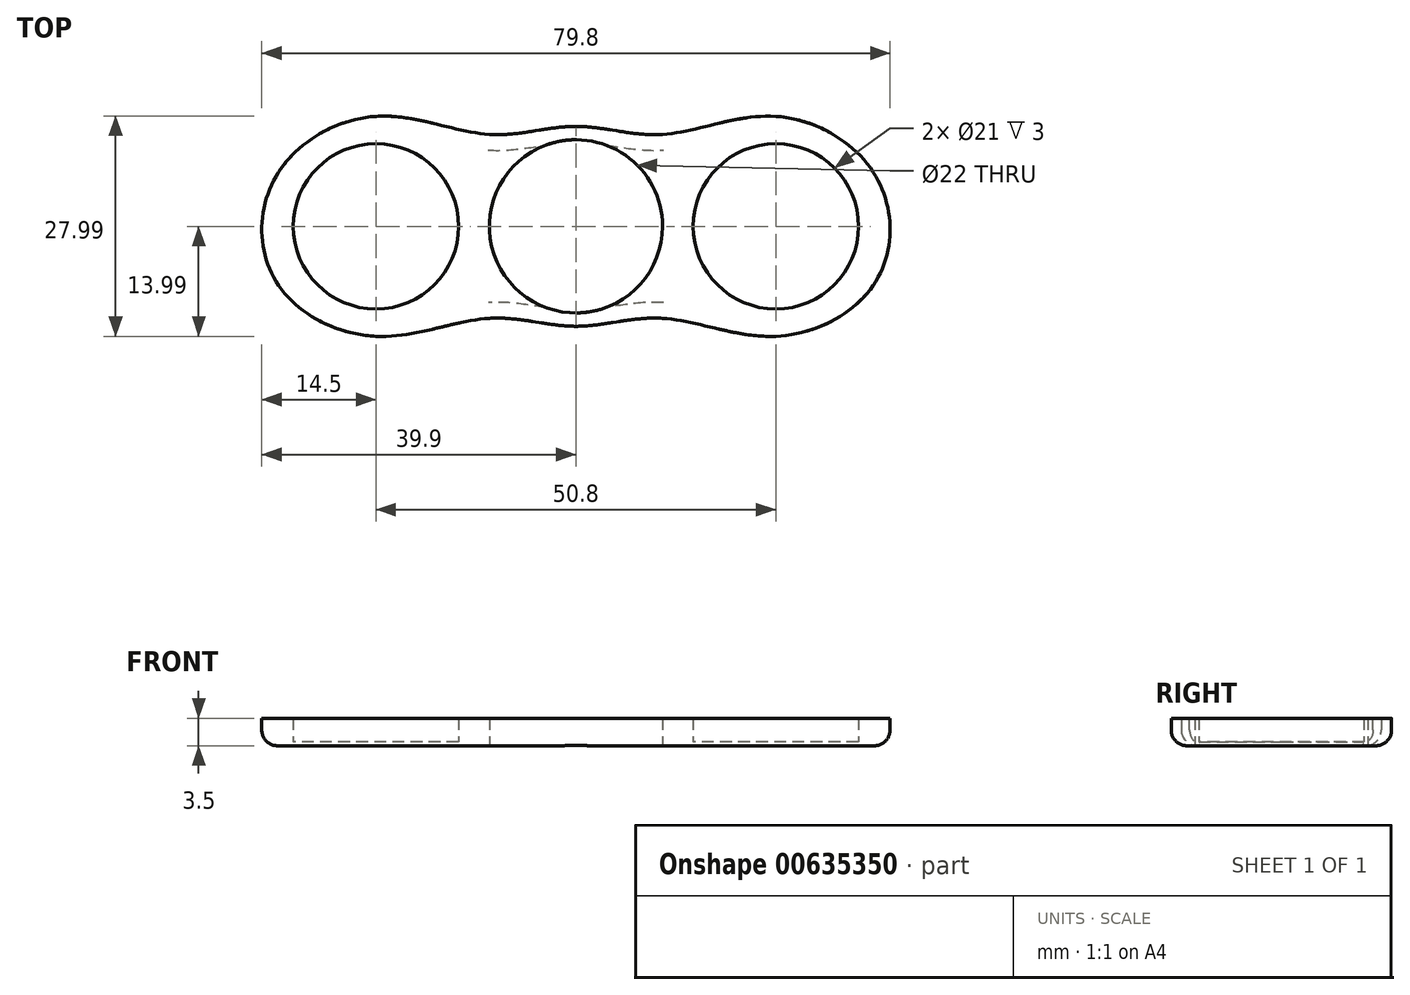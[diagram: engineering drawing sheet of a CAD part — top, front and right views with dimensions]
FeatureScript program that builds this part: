
annotation { "Feature Type Name" : "Feature", "Feature Type Description" : "" }
export const myFeature = defineFeature(function(context is Context, id is Id, definition is map)
    precondition{}
    {
        {
            var Q0;
            Q0=qCreatedBy(makeId("Top.planeOp"),FACE);
            var sketch = newSketch(context, id + "F0", { "sketchPlane" : qUnion([Q0])});
            skCircle(sketch, "E0", {"center": v(0, 0) * mm, "radius": 11 * mm});
            skLineSegment(sketch, "E1", {"start": v(0, 0) * mm, "end": v(25.4, 0) * mm});
            skLineSegment(sketch, "E2", {"start": v(0, 0) * mm, "end": v(-25.4, 0) * mm});
            skCircle(sketch, "E3", {"center": v(-25.4, 0) * mm, "radius": 10.5 * mm});
            skCircle(sketch, "E4", {"center": v(25.4, 0) * mm, "radius": 10.5 * mm});
            skLineSegment(sketch, "E5", {"start": v(-25.4, 0) * mm, "end": v(-25.4, -13.97) * mm});
            skLineSegment(sketch, "E6", {"start": v(25.4, 0) * mm, "end": v(25.4, -13.97) * mm});
            skLineSegment(sketch, "E7", {"start": v(-25.4, 0) * mm, "end": v(-25.4, 13.97) * mm});
            skLineSegment(sketch, "E8", {"start": v(25.4, 0) * mm, "end": v(25.4, 13.97) * mm});
            skLineSegment(sketch, "E9", {"start": v(0, 0) * mm, "end": v(0, -12.7) * mm});
            skLineSegment(sketch, "E10", {"start": v(0, 0) * mm, "end": v(0, 12.7) * mm});
            skLineSegment(sketch, "E11", {"start": v(0, 0) * mm, "end": v(0, -6.98) * mm});
            skPoint(sketch, "E11.endSnap0", {"position": v(25.4, -6.98) * mm});
            skLineSegment(sketch, "E12", {"start": v(0, 0) * mm, "end": v(0, 6.35) * mm});
            skLineSegment(sketch, "E13", {"start": v(0, -6.98) * mm, "end": v(38.1, -6.98) * mm});
            skLineSegment(sketch, "E14", {"start": v(38.1, 6.35) * mm, "end": v(0, 6.35) * mm});
            skLineSegment(sketch, "E15", {"start": v(0, 6.35) * mm, "end": v(-38.1, 6.35) * mm});
            skLineSegment(sketch, "E16", {"start": v(0, -6.98) * mm, "end": v(-38.1, -6.98) * mm});
            skLineSegment(sketch, "E17", {"start": v(-11, 0) * mm, "end": v(-11, -11.68) * mm});
            skPoint(sketch, "E17.startSnap0", {"position": v(-12.7, 0) * mm});
            skLineSegment(sketch, "E18", {"start": v(-11, -11.68) * mm, "end": v(-11, 0) * mm});
            skLineSegment(sketch, "E19", {"start": v(-11, 11.68) * mm, "end": v(-11, 0) * mm});
            skLineSegment(sketch, "E20", {"start": v(11, 0) * mm, "end": v(11, -11.68) * mm});
            skLineSegment(sketch, "E21", {"start": v(11, -11.68) * mm, "end": v(11, 0) * mm});
            skLineSegment(sketch, "E22", {"start": v(11, 11.68) * mm, "end": v(11, 0) * mm});
            skFitSpline(sketch, "E23", {"points": [v(0, 12.7) * mm, v(11, 11.68) * mm, v(25.4, 13.97) * mm, v(38.1, 6.35) * mm, v(38.1, -6.98) * mm, v(25.4, -13.97) * mm, v(11, -11.68) * mm, v(0, -12.7) * mm, v(-11, -11.68) * mm, v(-25.4, -13.97) * mm, v(-38.1, -6.99) * mm, v(-38.1, 6.35) * mm, v(-25.4, 13.97) * mm, v(-11, 11.68) * mm, v(0, 12.7) * mm]});
            skSolve(sketch);
        }
        {
            var Q0;
            {var subQ0=sQuery(id+"F0.wireOp",EDGE,"E15");var subQ1=sQuery(id+"F0.wireOp",EDGE,"E3");var subQ2=makeQuery(id+"F0.imprint","INTERSECT",VERTEX,{"disambiguationData":[OD(1.0)],"derivedFrom":[subQ1,subQ0]});Q0=makeQuery(id+"F0.imprint","IMPRINT",FACE,{"disambiguationData":[TD([[makeQuery(id+"F0.imprint","IMPRINT",EDGE,{"disambiguationData":[TD([[subQ2,-1.0]])],"derivedFrom":subQ1}),-1.0]])]});}
            var Q1;
            {var subQ0=sQuery(id+"F0.wireOp",EDGE,"E7");var subQ1=sQuery(id+"F0.wireOp",EDGE,"E3");var subQ2=makeQuery(id+"F0.imprint","INTERSECT",VERTEX,{"derivedFrom":[subQ1,subQ0]});Q1=makeQuery(id+"F0.imprint","IMPRINT",FACE,{"disambiguationData":[TD([[makeQuery(id+"F0.imprint","IMPRINT",EDGE,{"disambiguationData":[TD([[subQ2,-1.0]])],"derivedFrom":subQ1}),-1.0]])]});}
            var Q2;
            {var subQ0=sQuery(id+"F0.wireOp",EDGE,"E16");var subQ1=sQuery(id+"F0.wireOp",EDGE,"E3");var subQ2=makeQuery(id+"F0.imprint","INTERSECT",VERTEX,{"disambiguationData":[OD(0.0)],"derivedFrom":[subQ1,subQ0]});Q2=makeQuery(id+"F0.imprint","IMPRINT",FACE,{"disambiguationData":[TD([[makeQuery(id+"F0.imprint","IMPRINT",EDGE,{"disambiguationData":[TD([[subQ2,-1.0]])],"derivedFrom":subQ1}),-1.0]])]});}
            var Q3;
            {var subQ1=sQuery(id+"F0.wireOp",EDGE,"E3");var subQ7=sQuery(id+"F0.wireOp",EDGE,"E5");var subQ9=makeQuery(id+"F0.imprint","INTERSECT",VERTEX,{"derivedFrom":[subQ1,subQ7]});Q3=makeQuery(id+"F0.imprint","IMPRINT",FACE,{"disambiguationData":[TD([[makeQuery(id+"F0.imprint","IMPRINT",EDGE,{"disambiguationData":[TD([[subQ9,-1.0]])],"derivedFrom":subQ1}),-1.0]])]});}
            var Q4;
            {var subQ1=sQuery(id+"F0.wireOp",EDGE,"E2");var subQ3=sQuery(id+"F0.wireOp",EDGE,"E3");var subQ4=makeQuery(id+"F0.imprint","INTERSECT",VERTEX,{"derivedFrom":[subQ1,subQ3]});Q4=makeQuery(id+"F0.imprint","IMPRINT",FACE,{"disambiguationData":[TD([[makeQuery(id+"F0.imprint","IMPRINT",EDGE,{"disambiguationData":[TD([[subQ4,1.0]])],"derivedFrom":subQ3}),-1.0]])]});}
            var Q5;
            {var subQ1=sQuery(id+"F0.wireOp",EDGE,"E2");var subQ3=sQuery(id+"F0.wireOp",EDGE,"E3");var subQ4=makeQuery(id+"F0.imprint","INTERSECT",VERTEX,{"derivedFrom":[subQ1,subQ3]});Q5=makeQuery(id+"F0.imprint","IMPRINT",FACE,{"disambiguationData":[TD([[makeQuery(id+"F0.imprint","IMPRINT",EDGE,{"disambiguationData":[TD([[subQ4,-1.0]])],"derivedFrom":subQ3}),-1.0]])]});}
            var Q6;
            {var subQ3=sQuery(id+"F0.wireOp",EDGE,"E15");var subQ7=sQuery(id+"F0.wireOp",EDGE,"E3");var subQ9=makeQuery(id+"F0.imprint","INTERSECT",VERTEX,{"disambiguationData":[OD(0.0)],"derivedFrom":[subQ7,subQ3]});Q6=makeQuery(id+"F0.imprint","IMPRINT",FACE,{"disambiguationData":[TD([[makeQuery(id+"F0.imprint","IMPRINT",EDGE,{"disambiguationData":[TD([[subQ9,-1.0]])],"derivedFrom":subQ7}),-1.0]])]});}
            var Q7;
            {var subQ1=sQuery(id+"F0.wireOp",EDGE,"E0");var subQ6=sQuery(id+"F0.wireOp",EDGE,"E10");var subQ8=makeQuery(id+"F0.imprint","INTERSECT",VERTEX,{"derivedFrom":[subQ1,subQ6]});Q7=makeQuery(id+"F0.imprint","IMPRINT",FACE,{"disambiguationData":[TD([[makeQuery(id+"F0.imprint","IMPRINT",EDGE,{"disambiguationData":[TD([[subQ8,-1.0]])],"derivedFrom":subQ1}),-1.0]])]});}
            var Q8;
            {var subQ1=sQuery(id+"F0.wireOp",EDGE,"E0");var subQ3=sQuery(id+"F0.wireOp",EDGE,"E15");var subQ4=makeQuery(id+"F0.imprint","INTERSECT",VERTEX,{"derivedFrom":[subQ1,subQ3]});Q8=makeQuery(id+"F0.imprint","IMPRINT",FACE,{"disambiguationData":[TD([[makeQuery(id+"F0.imprint","IMPRINT",EDGE,{"disambiguationData":[TD([[subQ4,-1.0]])],"derivedFrom":subQ3}),1.0]])]});}
            var Q9;
            {var subQ1=sQuery(id+"F0.wireOp",EDGE,"E0");var subQ3=sQuery(id+"F0.wireOp",EDGE,"E16");var subQ4=makeQuery(id+"F0.imprint","INTERSECT",VERTEX,{"derivedFrom":[subQ1,subQ3]});Q9=makeQuery(id+"F0.imprint","IMPRINT",FACE,{"disambiguationData":[TD([[makeQuery(id+"F0.imprint","IMPRINT",EDGE,{"disambiguationData":[TD([[subQ4,-1.0]])],"derivedFrom":subQ3}),-1.0]])]});}
            var Q10;
            {var subQ3=sQuery(id+"F0.wireOp",EDGE,"E0");var subQ7=sQuery(id+"F0.wireOp",EDGE,"E16");var subQ9=makeQuery(id+"F0.imprint","INTERSECT",VERTEX,{"derivedFrom":[subQ3,subQ7]});Q10=makeQuery(id+"F0.imprint","IMPRINT",FACE,{"disambiguationData":[TD([[makeQuery(id+"F0.imprint","IMPRINT",EDGE,{"disambiguationData":[TD([[subQ9,-1.0]])],"derivedFrom":subQ3}),-1.0]])]});}
            var Q11;
            {var subQ5=sQuery(id+"F0.wireOp",EDGE,"E9");var subQ7=sQuery(id+"F0.wireOp",EDGE,"E0");var subQ8=makeQuery(id+"F0.imprint","INTERSECT",VERTEX,{"derivedFrom":[subQ7,subQ5]});Q11=makeQuery(id+"F0.imprint","IMPRINT",FACE,{"disambiguationData":[TD([[makeQuery(id+"F0.imprint","IMPRINT",EDGE,{"disambiguationData":[TD([[subQ8,-1.0]])],"derivedFrom":subQ7}),-1.0]])]});}
            var Q12;
            {var subQ1=sQuery(id+"F0.wireOp",EDGE,"E0");var subQ3=sQuery(id+"F0.wireOp",EDGE,"E13");var subQ4=makeQuery(id+"F0.imprint","INTERSECT",VERTEX,{"derivedFrom":[subQ1,subQ3]});Q12=makeQuery(id+"F0.imprint","IMPRINT",FACE,{"disambiguationData":[TD([[makeQuery(id+"F0.imprint","IMPRINT",EDGE,{"disambiguationData":[TD([[subQ4,-1.0]])],"derivedFrom":subQ3}),1.0]])]});}
            var Q13;
            {var subQ1=sQuery(id+"F0.wireOp",EDGE,"E0");var subQ3=sQuery(id+"F0.wireOp",EDGE,"E14");var subQ4=makeQuery(id+"F0.imprint","INTERSECT",VERTEX,{"derivedFrom":[subQ1,subQ3]});Q13=makeQuery(id+"F0.imprint","IMPRINT",FACE,{"disambiguationData":[TD([[makeQuery(id+"F0.imprint","IMPRINT",EDGE,{"disambiguationData":[TD([[subQ4,1.0]])],"derivedFrom":subQ3}),1.0]])]});}
            var Q14;
            {var subQ3=sQuery(id+"F0.wireOp",EDGE,"E0");var subQ7=sQuery(id+"F0.wireOp",EDGE,"E14");var subQ9=makeQuery(id+"F0.imprint","INTERSECT",VERTEX,{"derivedFrom":[subQ3,subQ7]});Q14=makeQuery(id+"F0.imprint","IMPRINT",FACE,{"disambiguationData":[TD([[makeQuery(id+"F0.imprint","IMPRINT",EDGE,{"disambiguationData":[TD([[subQ9,-1.0]])],"derivedFrom":subQ3}),-1.0]])]});}
            var Q15;
            {var subQ5=sQuery(id+"F0.wireOp",EDGE,"E4");var subQ7=sQuery(id+"F0.wireOp",EDGE,"E8");var subQ8=makeQuery(id+"F0.imprint","INTERSECT",VERTEX,{"derivedFrom":[subQ5,subQ7]});Q15=makeQuery(id+"F0.imprint","IMPRINT",FACE,{"disambiguationData":[TD([[makeQuery(id+"F0.imprint","IMPRINT",EDGE,{"disambiguationData":[TD([[subQ8,-1.0]])],"derivedFrom":subQ5}),-1.0]])]});}
            var Q16;
            {var subQ1=sQuery(id+"F0.wireOp",EDGE,"E1");var subQ3=sQuery(id+"F0.wireOp",EDGE,"E4");var subQ4=makeQuery(id+"F0.imprint","INTERSECT",VERTEX,{"derivedFrom":[subQ1,subQ3]});Q16=makeQuery(id+"F0.imprint","IMPRINT",FACE,{"disambiguationData":[TD([[makeQuery(id+"F0.imprint","IMPRINT",EDGE,{"disambiguationData":[TD([[subQ4,1.0]])],"derivedFrom":subQ3}),-1.0]])]});}
            var Q17;
            {var subQ1=sQuery(id+"F0.wireOp",EDGE,"E1");var subQ3=sQuery(id+"F0.wireOp",EDGE,"E4");var subQ4=makeQuery(id+"F0.imprint","INTERSECT",VERTEX,{"derivedFrom":[subQ1,subQ3]});Q17=makeQuery(id+"F0.imprint","IMPRINT",FACE,{"disambiguationData":[TD([[makeQuery(id+"F0.imprint","IMPRINT",EDGE,{"disambiguationData":[TD([[subQ4,-1.0]])],"derivedFrom":subQ3}),-1.0]])]});}
            var Q18;
            {var subQ3=sQuery(id+"F0.wireOp",EDGE,"E13");var subQ5=sQuery(id+"F0.wireOp",EDGE,"E4");var subQ6=makeQuery(id+"F0.imprint","INTERSECT",VERTEX,{"disambiguationData":[OD(0.0)],"derivedFrom":[subQ5,subQ3]});Q18=makeQuery(id+"F0.imprint","IMPRINT",FACE,{"disambiguationData":[TD([[makeQuery(id+"F0.imprint","IMPRINT",EDGE,{"disambiguationData":[TD([[subQ6,-1.0]])],"derivedFrom":subQ5}),-1.0]])]});}
            var Q19;
            {var subQ0=sQuery(id+"F0.wireOp",EDGE,"E6");var subQ1=sQuery(id+"F0.wireOp",EDGE,"E4");var subQ2=makeQuery(id+"F0.imprint","INTERSECT",VERTEX,{"derivedFrom":[subQ1,subQ0]});Q19=makeQuery(id+"F0.imprint","IMPRINT",FACE,{"disambiguationData":[TD([[makeQuery(id+"F0.imprint","IMPRINT",EDGE,{"disambiguationData":[TD([[subQ2,-1.0]])],"derivedFrom":subQ1}),-1.0]])]});}
            var Q20;
            {var subQ0=sQuery(id+"F0.wireOp",EDGE,"E14");var subQ1=sQuery(id+"F0.wireOp",EDGE,"E4");var subQ2=makeQuery(id+"F0.imprint","INTERSECT",VERTEX,{"disambiguationData":[OD(0.0)],"derivedFrom":[subQ1,subQ0]});Q20=makeQuery(id+"F0.imprint","IMPRINT",FACE,{"disambiguationData":[TD([[makeQuery(id+"F0.imprint","IMPRINT",EDGE,{"disambiguationData":[TD([[subQ2,1.0]])],"derivedFrom":subQ1}),-1.0]])]});}
            var Q21;
            {var subQ0=sQuery(id+"F0.wireOp",EDGE,"E8");var subQ1=sQuery(id+"F0.wireOp",EDGE,"E4");var subQ2=makeQuery(id+"F0.imprint","INTERSECT",VERTEX,{"derivedFrom":[subQ1,subQ0]});Q21=makeQuery(id+"F0.imprint","IMPRINT",FACE,{"disambiguationData":[TD([[makeQuery(id+"F0.imprint","IMPRINT",EDGE,{"disambiguationData":[TD([[subQ2,1.0]])],"derivedFrom":subQ1}),-1.0]])]});}
            extrude(context, id + "F1", {"entities" : qUnion([Q0, Q1, Q2, Q3, Q4, Q5, Q6, Q7, Q8, Q9, Q10, Q11, Q12, Q13, Q14, Q15, Q16, Q17, Q18, Q19, Q20, Q21]), "depth" : 3.5 * mm, "offsetDistance" : 25.4 * mm});
        }
        {
            var Q0;
            Q0 = qSketchRegion(id + "F0", true);
            var Q1;
            {var subQ3=sQuery(id+"F0.wireOp",EDGE,"E15");var subQ7=sQuery(id+"F0.wireOp",EDGE,"E3");var subQ8=makeQuery(id+"F0.imprint","INTERSECT",VERTEX,{"disambiguationData":[OD(1.0)],"derivedFrom":[subQ7,subQ3]});Q1=makeQuery(id+"F0.imprint","IMPRINT",FACE,{"disambiguationData":[TD([[makeQuery(id+"F0.imprint","IMPRINT",EDGE,{"disambiguationData":[TD([[subQ8,-1.0]])],"derivedFrom":subQ7}),1.0]])]});}
            var Q2;
            {var subQ0=sQuery(id+"F0.wireOp",EDGE,"E7");var subQ1=sQuery(id+"F0.wireOp",EDGE,"E3");var subQ2=makeQuery(id+"F0.imprint","INTERSECT",VERTEX,{"derivedFrom":[subQ1,subQ0]});Q2=makeQuery(id+"F0.imprint","IMPRINT",FACE,{"disambiguationData":[TD([[makeQuery(id+"F0.imprint","IMPRINT",EDGE,{"disambiguationData":[TD([[subQ2,-1.0]])],"derivedFrom":subQ1}),1.0]])]});}
            var Q3;
            {var subQ0=sQuery(id+"F0.wireOp",EDGE,"E15");var subQ1=sQuery(id+"F0.wireOp",EDGE,"E3");var subQ2=makeQuery(id+"F0.imprint","INTERSECT",VERTEX,{"disambiguationData":[OD(0.0)],"derivedFrom":[subQ1,subQ0]});Q3=makeQuery(id+"F0.imprint","IMPRINT",FACE,{"disambiguationData":[TD([[makeQuery(id+"F0.imprint","IMPRINT",EDGE,{"disambiguationData":[TD([[subQ2,-1.0]])],"derivedFrom":subQ1}),1.0]])]});}
            var Q4;
            {var subQ1=sQuery(id+"F0.wireOp",EDGE,"E2");var subQ3=sQuery(id+"F0.wireOp",EDGE,"E3");var subQ4=makeQuery(id+"F0.imprint","INTERSECT",VERTEX,{"derivedFrom":[subQ1,subQ3]});Q4=makeQuery(id+"F0.imprint","IMPRINT",FACE,{"disambiguationData":[TD([[makeQuery(id+"F0.imprint","IMPRINT",EDGE,{"disambiguationData":[TD([[subQ4,-1.0]])],"derivedFrom":subQ3}),1.0]])]});}
            var Q5;
            {var subQ1=sQuery(id+"F0.wireOp",EDGE,"E2");var subQ3=sQuery(id+"F0.wireOp",EDGE,"E3");var subQ4=makeQuery(id+"F0.imprint","INTERSECT",VERTEX,{"derivedFrom":[subQ1,subQ3]});Q5=makeQuery(id+"F0.imprint","IMPRINT",FACE,{"disambiguationData":[TD([[makeQuery(id+"F0.imprint","IMPRINT",EDGE,{"disambiguationData":[TD([[subQ4,1.0]])],"derivedFrom":subQ3}),1.0]])]});}
            var Q6;
            {var subQ0=sQuery(id+"F0.wireOp",EDGE,"E5");var subQ1=sQuery(id+"F0.wireOp",EDGE,"E3");var subQ2=makeQuery(id+"F0.imprint","INTERSECT",VERTEX,{"derivedFrom":[subQ1,subQ0]});Q6=makeQuery(id+"F0.imprint","IMPRINT",FACE,{"disambiguationData":[TD([[makeQuery(id+"F0.imprint","IMPRINT",EDGE,{"disambiguationData":[TD([[subQ2,-1.0]])],"derivedFrom":subQ1}),1.0]])]});}
            var Q7;
            {var subQ0=sQuery(id+"F0.wireOp",EDGE,"E16");var subQ1=sQuery(id+"F0.wireOp",EDGE,"E3");var subQ2=makeQuery(id+"F0.imprint","INTERSECT",VERTEX,{"disambiguationData":[OD(0.0)],"derivedFrom":[subQ1,subQ0]});Q7=makeQuery(id+"F0.imprint","IMPRINT",FACE,{"disambiguationData":[TD([[makeQuery(id+"F0.imprint","IMPRINT",EDGE,{"disambiguationData":[TD([[subQ2,-1.0]])],"derivedFrom":subQ1}),1.0]])]});}
            var Q8;
            {var subQ0=sQuery(id+"F0.wireOp",EDGE,"E8");var subQ1=sQuery(id+"F0.wireOp",EDGE,"E4");var subQ2=makeQuery(id+"F0.imprint","INTERSECT",VERTEX,{"derivedFrom":[subQ1,subQ0]});Q8=makeQuery(id+"F0.imprint","IMPRINT",FACE,{"disambiguationData":[TD([[makeQuery(id+"F0.imprint","IMPRINT",EDGE,{"disambiguationData":[TD([[subQ2,-1.0]])],"derivedFrom":subQ1}),1.0]])]});}
            var Q9;
            {var subQ1=sQuery(id+"F0.wireOp",EDGE,"E1");var subQ3=sQuery(id+"F0.wireOp",EDGE,"E4");var subQ4=makeQuery(id+"F0.imprint","INTERSECT",VERTEX,{"derivedFrom":[subQ1,subQ3]});Q9=makeQuery(id+"F0.imprint","IMPRINT",FACE,{"disambiguationData":[TD([[makeQuery(id+"F0.imprint","IMPRINT",EDGE,{"disambiguationData":[TD([[subQ4,1.0]])],"derivedFrom":subQ3}),1.0]])]});}
            var Q10;
            {var subQ1=sQuery(id+"F0.wireOp",EDGE,"E1");var subQ3=sQuery(id+"F0.wireOp",EDGE,"E4");var subQ4=makeQuery(id+"F0.imprint","INTERSECT",VERTEX,{"derivedFrom":[subQ1,subQ3]});Q10=makeQuery(id+"F0.imprint","IMPRINT",FACE,{"disambiguationData":[TD([[makeQuery(id+"F0.imprint","IMPRINT",EDGE,{"disambiguationData":[TD([[subQ4,-1.0]])],"derivedFrom":subQ3}),1.0]])]});}
            var Q11;
            {var subQ0=sQuery(id+"F0.wireOp",EDGE,"E13");var subQ1=sQuery(id+"F0.wireOp",EDGE,"E4");var subQ2=makeQuery(id+"F0.imprint","INTERSECT",VERTEX,{"disambiguationData":[OD(0.0)],"derivedFrom":[subQ1,subQ0]});Q11=makeQuery(id+"F0.imprint","IMPRINT",FACE,{"disambiguationData":[TD([[makeQuery(id+"F0.imprint","IMPRINT",EDGE,{"disambiguationData":[TD([[subQ2,-1.0]])],"derivedFrom":subQ1}),1.0]])]});}
            var Q12;
            {var subQ0=sQuery(id+"F0.wireOp",EDGE,"E6");var subQ1=sQuery(id+"F0.wireOp",EDGE,"E4");var subQ2=makeQuery(id+"F0.imprint","INTERSECT",VERTEX,{"derivedFrom":[subQ1,subQ0]});Q12=makeQuery(id+"F0.imprint","IMPRINT",FACE,{"disambiguationData":[TD([[makeQuery(id+"F0.imprint","IMPRINT",EDGE,{"disambiguationData":[TD([[subQ2,-1.0]])],"derivedFrom":subQ1}),1.0]])]});}
            var Q13;
            {var subQ1=sQuery(id+"F0.wireOp",EDGE,"E4");var subQ7=sQuery(id+"F0.wireOp",EDGE,"E14");var subQ8=makeQuery(id+"F0.imprint","INTERSECT",VERTEX,{"disambiguationData":[OD(0.0)],"derivedFrom":[subQ1,subQ7]});Q13=makeQuery(id+"F0.imprint","IMPRINT",FACE,{"disambiguationData":[TD([[makeQuery(id+"F0.imprint","IMPRINT",EDGE,{"disambiguationData":[TD([[subQ8,1.0]])],"derivedFrom":subQ1}),1.0]])]});}
            var Q14;
            {var subQ0=sQuery(id+"F0.wireOp",EDGE,"E8");var subQ1=sQuery(id+"F0.wireOp",EDGE,"E4");var subQ2=makeQuery(id+"F0.imprint","INTERSECT",VERTEX,{"derivedFrom":[subQ1,subQ0]});Q14=makeQuery(id+"F0.imprint","IMPRINT",FACE,{"disambiguationData":[TD([[makeQuery(id+"F0.imprint","IMPRINT",EDGE,{"disambiguationData":[TD([[subQ2,1.0]])],"derivedFrom":subQ1}),1.0]])]});}
            extrude(context, id + "F2", {"entities" : qUnion([Q0, Q1, Q2, Q3, Q4, Q5, Q6, Q7, Q8, Q9, Q10, Q11, Q12, Q13, Q14]), "operationType" : NewBodyOperationType.ADD, "depth" : .5 * mm, "offsetDistance" : 25.4 * mm});
        }
        {
            var Q0;
            Q0=makeQuery(id+"F1.opExtrude","CAP_EDGE",EDGE,{"disambiguationData":[OSD([sQuery(id+"F0.wireOp",EDGE,"E23")])],"isStart":true});
            fillet(context, id + "F3", {"entities" : qUnion([Q0]), "radius" : 2 * mm, "tangentPropagation" : true, "allowEdgeOverflow" : false});
        }
    });
